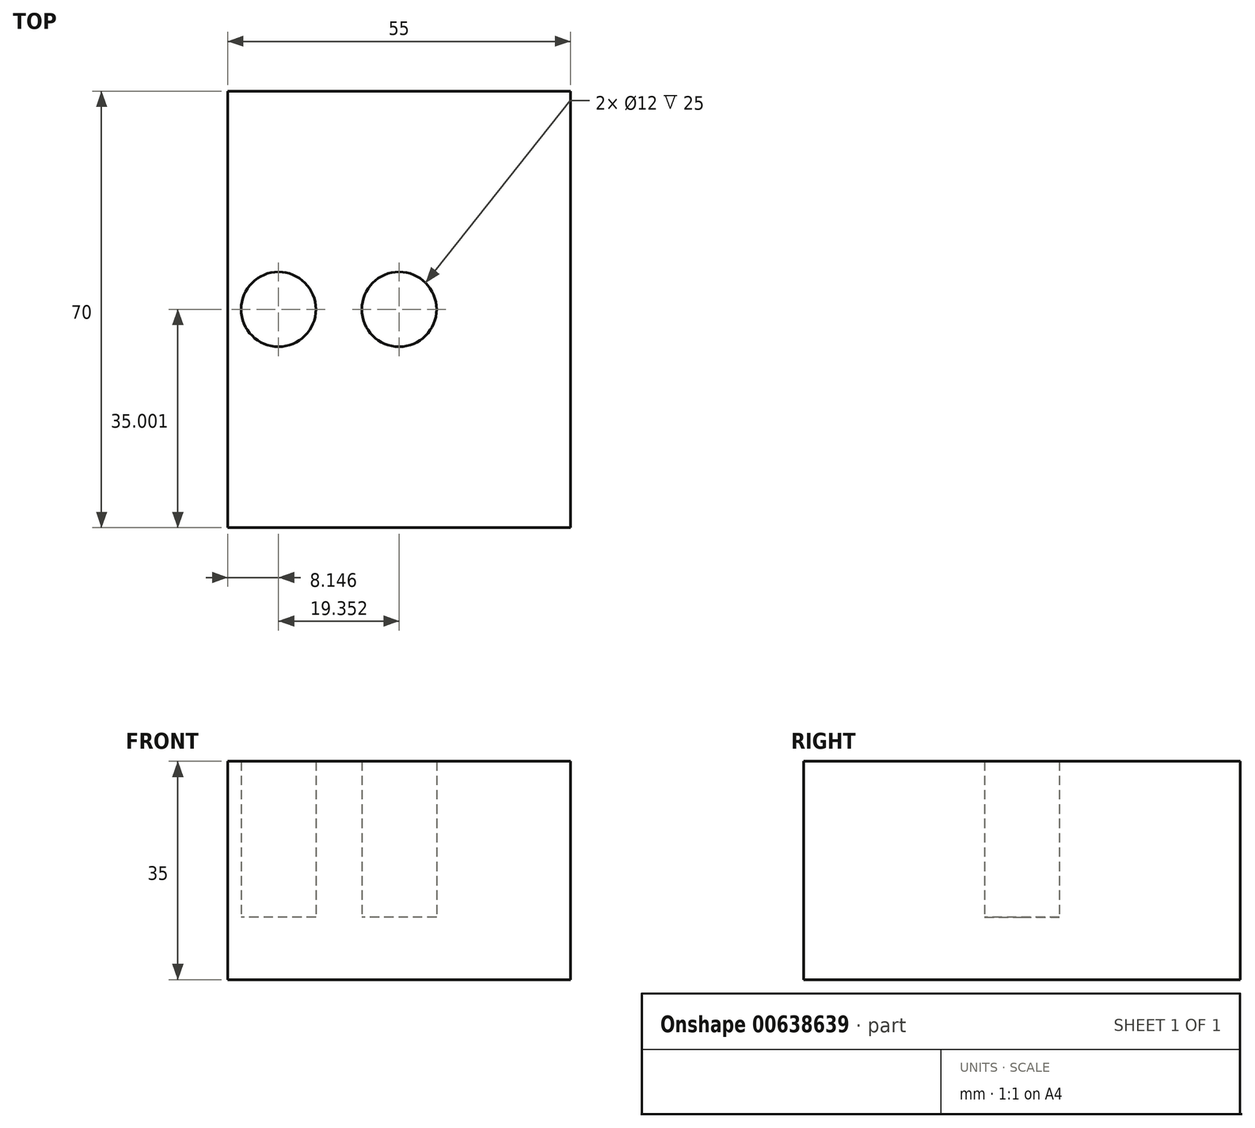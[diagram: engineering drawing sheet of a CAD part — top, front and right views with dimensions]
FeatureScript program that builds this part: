
annotation { "Feature Type Name" : "Feature", "Feature Type Description" : "" }
export const myFeature = defineFeature(function(context is Context, id is Id, definition is map)
    precondition{}
    {
        {
            var Q0;
            Q0=qCreatedBy(makeId("Top.planeOp"),FACE);
            var sketch = newSketch(context, id + "F0", { "sketchPlane" : qUnion([Q0])});
            skLineSegment(sketch, "E0.bottom", {"start": v(-43.94, 47.8) * mm, "end": v(11.06, 47.8) * mm});
            skLineSegment(sketch, "E0.top", {"start": v(-43.94, -22.2) * mm, "end": v(11.06, -22.2) * mm});
            skLineSegment(sketch, "E0.left", {"start": v(-43.94, 47.8) * mm, "end": v(-43.94, -22.2) * mm});
            skLineSegment(sketch, "E0.right", {"start": v(11.06, 47.8) * mm, "end": v(11.06, -22.2) * mm});
            skSolve(sketch);
        }
        {
            var Q0;
            Q0=makeQuery(id+"F0.imprint","IMPRINT",FACE,{"disambiguationData":[TD([[makeQuery(id+"F0.imprint","IMPRINT",EDGE,{"derivedFrom":sQuery(id+"F0.wireOp",EDGE,"E0.bottom")}),-1.0]])]});
            extrude(context, id + "F1", {"entities" : qUnion([Q0]), "depth" : -10 * mm, "offsetDistance" : 25 * mm});
        }
        {
            var Q0;
            Q0=makeQuery(id+"F1.opExtrude","CAP_FACE",FACE,{"disambiguationData":[OSD([sQuery(id+"F0.wireOp",EDGE,"E0.bottom"),sQuery(id+"F0.wireOp",EDGE,"E0.top"),sQuery(id+"F0.wireOp",EDGE,"E0.left"),sQuery(id+"F0.wireOp",EDGE,"E0.right")])],"isStart":true});
            var sketch = newSketch(context, id + "F2", { "sketchPlane" : qUnion([Q0])});
            skLineSegment(sketch, "E1", {"start": v(-43.94, 12.8) * mm, "end": v(11.06, 12.8) * mm});
            skLineSegment(sketch, "E2", {"start": v(-16.44, 12.8) * mm, "end": v(-35.8, 12.8) * mm, "construction": true});
            skLineSegment(sketch, "E3", {"start": v(-16.44, 12.8) * mm, "end": v(3.06, 12.8) * mm, "construction": true});
            skCircle(sketch, "E4", {"center": v(-35.8, 12.8) * mm, "radius": 6 * mm});
            skCircle(sketch, "E5", {"center": v(-16.44, 12.8) * mm, "radius": 6 * mm});
            skCircle(sketch, "E6", {"center": v(3.06, 12.8) * mm, "radius": 6 * mm});
            skSolve(sketch);
        }
        {
            var Q0;
            {var subQ0=sQuery(id+"F2.wireOp",EDGE,"E4");var subQ1=sQuery(id+"F2.wireOp",EDGE,"E1");var subQ2=makeQuery(id+"F2.imprint","INTERSECT",VERTEX,{"disambiguationData":[OD(0.0)],"derivedFrom":[subQ1,subQ0]});Q0=makeQuery(id+"F2.imprint","IMPRINT",FACE,{"disambiguationData":[TD([[makeQuery(id+"F2.imprint","IMPRINT",EDGE,{"disambiguationData":[TD([[subQ2,-1.0]])],"derivedFrom":subQ1}),1.0]])]});}
            var Q1;
            {var subQ0=sQuery(id+"F2.wireOp",EDGE,"E4");var subQ1=sQuery(id+"F2.wireOp",EDGE,"E1");var subQ2=makeQuery(id+"F2.imprint","INTERSECT",VERTEX,{"disambiguationData":[OD(0.0)],"derivedFrom":[subQ1,subQ0]});Q1=makeQuery(id+"F2.imprint","IMPRINT",FACE,{"disambiguationData":[TD([[makeQuery(id+"F2.imprint","IMPRINT",EDGE,{"disambiguationData":[TD([[subQ2,-1.0]])],"derivedFrom":subQ1}),-1.0]])]});}
            var Q2;
            {var subQ0=sQuery(id+"F2.wireOp",EDGE,"E5");var subQ1=sQuery(id+"F2.wireOp",EDGE,"E1");var subQ2=makeQuery(id+"F2.imprint","INTERSECT",VERTEX,{"disambiguationData":[OD(0.0)],"derivedFrom":[subQ1,subQ0]});Q2=makeQuery(id+"F2.imprint","IMPRINT",FACE,{"disambiguationData":[TD([[makeQuery(id+"F2.imprint","IMPRINT",EDGE,{"disambiguationData":[TD([[subQ2,-1.0]])],"derivedFrom":subQ1}),1.0]])]});}
            var Q3;
            {var subQ0=sQuery(id+"F2.wireOp",EDGE,"E5");var subQ1=sQuery(id+"F2.wireOp",EDGE,"E1");var subQ2=makeQuery(id+"F2.imprint","INTERSECT",VERTEX,{"disambiguationData":[OD(0.0)],"derivedFrom":[subQ1,subQ0]});Q3=makeQuery(id+"F2.imprint","IMPRINT",FACE,{"disambiguationData":[TD([[makeQuery(id+"F2.imprint","IMPRINT",EDGE,{"disambiguationData":[TD([[subQ2,-1.0]])],"derivedFrom":subQ1}),-1.0]])]});}
            var Q4;
            {var subQ0=sQuery(id+"F2.wireOp",EDGE,"E6");var subQ1=sQuery(id+"F2.wireOp",EDGE,"E1");var subQ2=makeQuery(id+"F2.imprint","INTERSECT",VERTEX,{"disambiguationData":[OD(0.0)],"derivedFrom":[subQ1,subQ0]});Q4=makeQuery(id+"F2.imprint","IMPRINT",FACE,{"disambiguationData":[TD([[makeQuery(id+"F2.imprint","IMPRINT",EDGE,{"disambiguationData":[TD([[subQ2,-1.0]])],"derivedFrom":subQ1}),1.0]])]});}
            var Q5;
            {var subQ0=sQuery(id+"F2.wireOp",EDGE,"E6");var subQ1=sQuery(id+"F2.wireOp",EDGE,"E1");var subQ2=makeQuery(id+"F2.imprint","INTERSECT",VERTEX,{"disambiguationData":[OD(0.0)],"derivedFrom":[subQ1,subQ0]});Q5=makeQuery(id+"F2.imprint","IMPRINT",FACE,{"disambiguationData":[TD([[makeQuery(id+"F2.imprint","IMPRINT",EDGE,{"disambiguationData":[TD([[subQ2,-1.0]])],"derivedFrom":subQ1}),-1.0]])]});}
            extrude(context, id + "F3", {"entities" : qUnion([Q0, Q1, Q2, Q3, Q4, Q5]), "operationType" : NewBodyOperationType.ADD, "depth" : 25 * mm, "offsetDistance" : 25 * mm});
        }
    });
